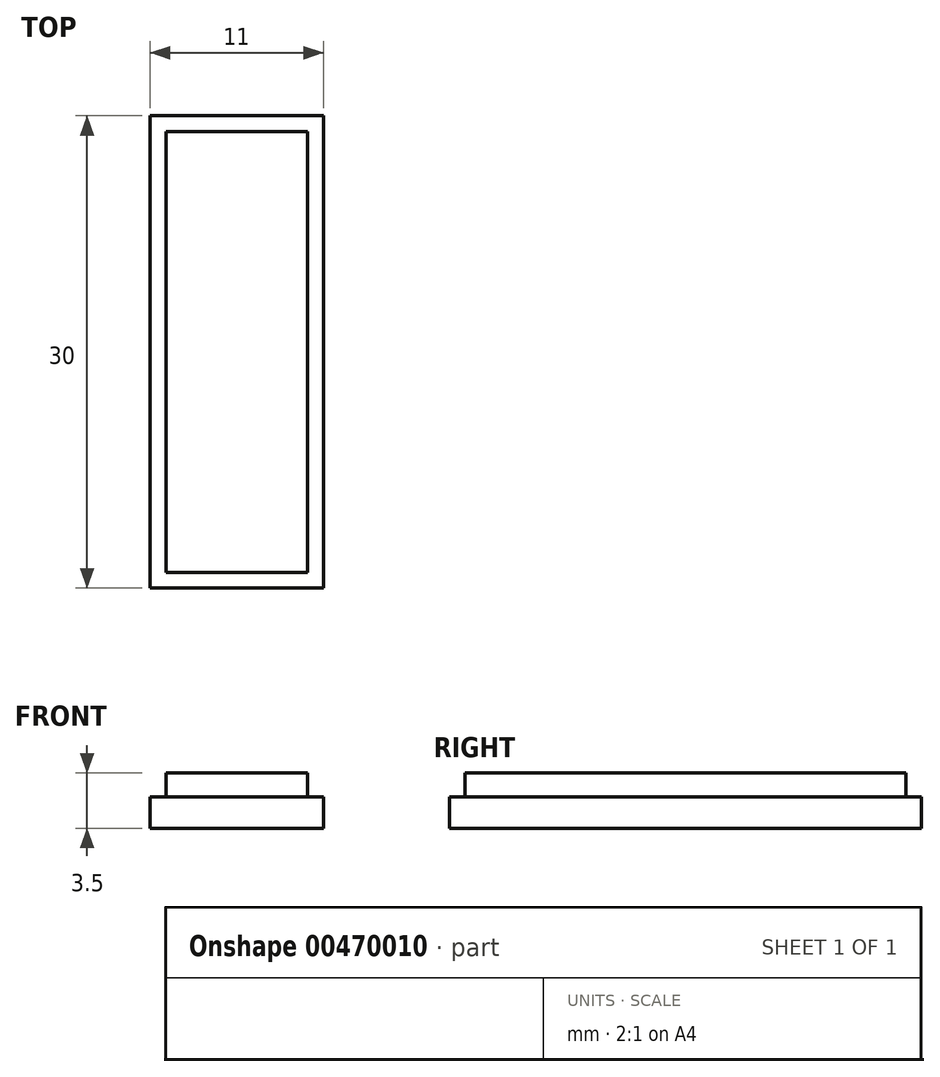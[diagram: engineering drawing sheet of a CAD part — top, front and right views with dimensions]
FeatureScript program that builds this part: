
annotation { "Feature Type Name" : "Feature", "Feature Type Description" : "" }
export const myFeature = defineFeature(function(context is Context, id is Id, definition is map)
    precondition{}
    {
        {
            var Q0;
            Q0=qCreatedBy(makeId("Top.planeOp"),FACE);
            var sketch = newSketch(context, id + "F0", { "sketchPlane" : qUnion([Q0])});
            skLineSegment(sketch, "E0.bottom", {"start": v(5.5, -15) * mm, "end": v(-5.5, -15) * mm});
            skLineSegment(sketch, "E0.top", {"start": v(5.5, 15) * mm, "end": v(-5.5, 15) * mm});
            skLineSegment(sketch, "E0.left", {"start": v(5.5, -15) * mm, "end": v(5.5, 15) * mm});
            skLineSegment(sketch, "E0.right", {"start": v(-5.5, -15) * mm, "end": v(-5.5, 15) * mm});
            skPoint(sketch, "E0.middle", {"position": v(0, 0) * mm});
            skLineSegment(sketch, "E1.bottom", {"start": v(4.5, -14) * mm, "end": v(-4.5, -14) * mm});
            skLineSegment(sketch, "E1.top", {"start": v(4.5, 14) * mm, "end": v(-4.5, 14) * mm});
            skLineSegment(sketch, "E1.left", {"start": v(4.5, -14) * mm, "end": v(4.5, 14) * mm});
            skLineSegment(sketch, "E1.right", {"start": v(-4.5, -14) * mm, "end": v(-4.5, 14) * mm});
            skSolve(sketch);
        }
        {
            var Q0;
            Q0=makeQuery(id+"F0.imprint","IMPRINT",FACE,{"disambiguationData":[TD([[makeQuery(id+"F0.imprint","IMPRINT",EDGE,{"derivedFrom":sQuery(id+"F0.wireOp",EDGE,"E0.bottom")}),-1.0]])]});
            var Q1;
            Q1=makeQuery(id+"F0.imprint","IMPRINT",FACE,{"disambiguationData":[TD([[makeQuery(id+"F0.imprint","IMPRINT",EDGE,{"derivedFrom":sQuery(id+"F0.wireOp",EDGE,"E1.bottom")}),-1.0]])]});
            extrude(context, id + "F1", {"entities" : qUnion([Q0, Q1]), "oppositeDirection" : true, "depth" : 2 * mm, "offsetDistance" : 25 * mm});
        }
        {
            var Q0;
            Q0=makeQuery(id+"F1.opExtrude","CAP_FACE",FACE,{"disambiguationData":[OSD([sQuery(id+"F0.wireOp",EDGE,"E0.bottom"),sQuery(id+"F0.wireOp",EDGE,"E0.top"),sQuery(id+"F0.wireOp",EDGE,"E0.left"),sQuery(id+"F0.wireOp",EDGE,"E0.right")])],"isStart":true});
            var sketch = newSketch(context, id + "F2", { "sketchPlane" : qUnion([Q0])});
            skLineSegment(sketch, "E2.bottom", {"start": v(4.5, 14) * mm, "end": v(-4.5, 14) * mm});
            skLineSegment(sketch, "E2.top", {"start": v(4.5, -14) * mm, "end": v(-4.5, -14) * mm});
            skLineSegment(sketch, "E2.left", {"start": v(4.5, 14) * mm, "end": v(4.5, -14) * mm});
            skLineSegment(sketch, "E2.right", {"start": v(-4.5, 14) * mm, "end": v(-4.5, -14) * mm});
            skPoint(sketch, "E2.middle", {"position": v(0, 0) * mm});
            skSolve(sketch);
        }
        {
            var Q0;
            Q0 = qSketchRegion(id + "F2", true);
            extrude(context, id + "F3", {"entities" : qUnion([Q0]), "operationType" : NewBodyOperationType.ADD, "depth" : 1.5 * mm, "offsetDistance" : 25 * mm});
        }
    });
